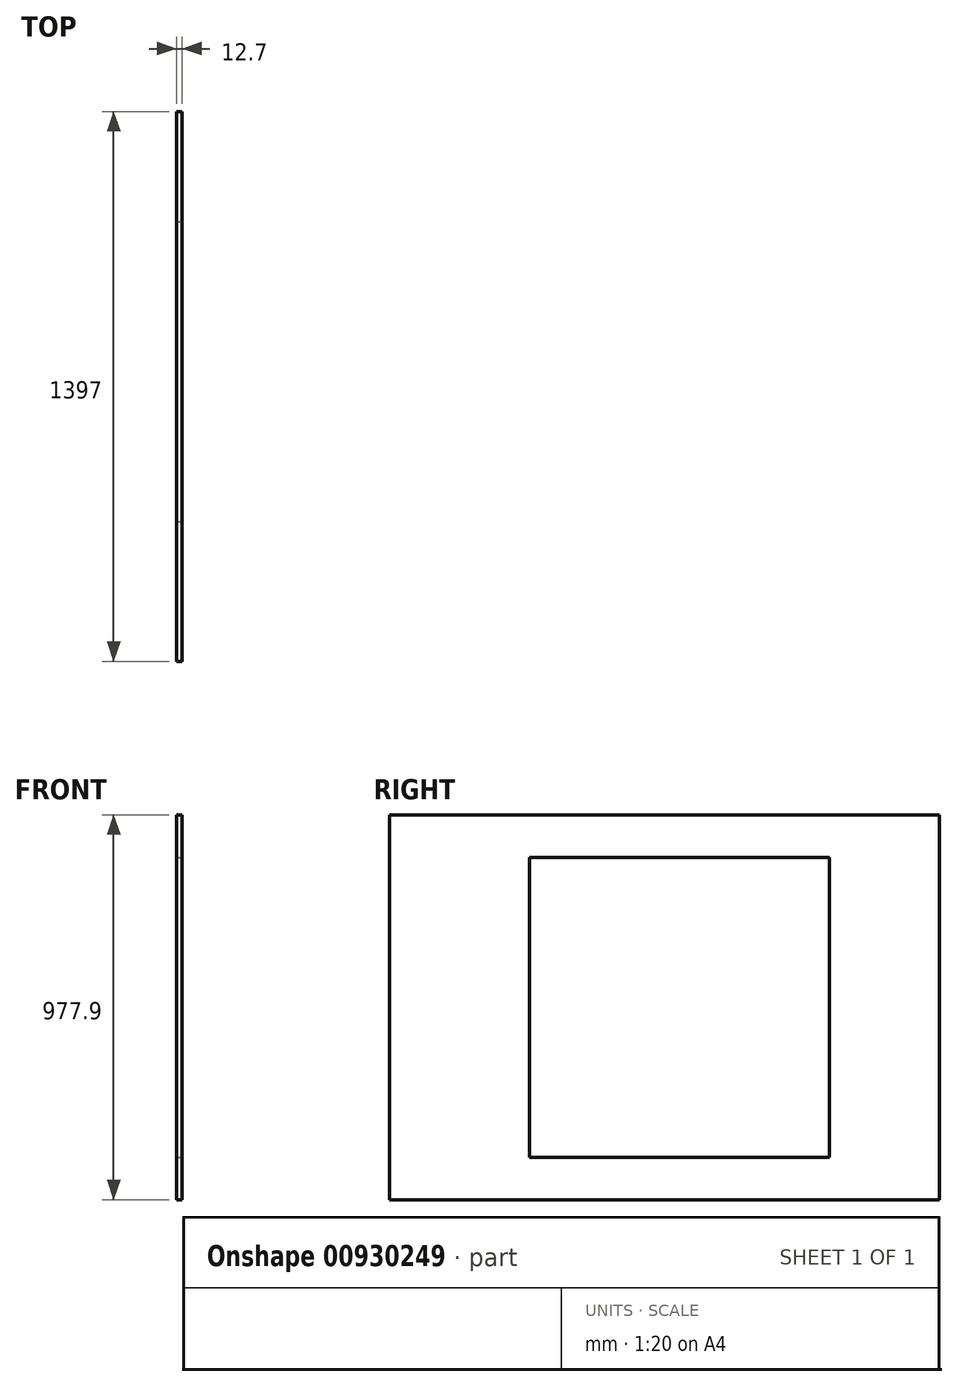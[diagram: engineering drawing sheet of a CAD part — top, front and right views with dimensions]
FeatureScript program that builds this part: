
annotation { "Feature Type Name" : "Feature", "Feature Type Description" : "" }
export const myFeature = defineFeature(function(context is Context, id is Id, definition is map)
    precondition{}
    {
        {
            var Q0;
            Q0=qCreatedBy(makeId("Right.planeOp"),FACE);
            var sketch = newSketch(context, id + "F0", { "sketchPlane" : qUnion([Q0])});
            skLineSegment(sketch, "E0.bottom", {"start": v(698.5, -488.95) * mm, "end": v(-698.5, -488.95) * mm});
            skLineSegment(sketch, "E0.top", {"start": v(698.5, 488.95) * mm, "end": v(-698.5, 488.95) * mm});
            skLineSegment(sketch, "E0.left", {"start": v(698.5, -488.95) * mm, "end": v(698.5, 488.95) * mm});
            skLineSegment(sketch, "E0.right", {"start": v(-698.5, -488.95) * mm, "end": v(-698.5, 488.95) * mm});
            skPoint(sketch, "E0.middle", {"position": v(0, 0) * mm});
            skSolve(sketch);
        }
        {
            var Q0;
            Q0=qSketchRegion(id+"F0",true);
            extrude(context, id + "F1", {"entities" : qUnion([Q0]), "endBound" : BoundingType.SYMMETRIC, "depth" : 12.7 * mm});
        }
        {
            var Q0;
            Q0=makeQuery(id+"F1.opExtrude","CAP_FACE",FACE,{"disambiguationData":[OSD([sQuery(id+"F0.wireOp",EDGE,"E0.bottom"),sQuery(id+"F0.wireOp",EDGE,"E0.top"),sQuery(id+"F0.wireOp",EDGE,"E0.left"),sQuery(id+"F0.wireOp",EDGE,"E0.right")])],"isStart":false});
            var sketch = newSketch(context, id + "F2", { "sketchPlane" : qUnion([Q0])});
            skLineSegment(sketch, "E1.bottom", {"start": v(-342.9, -381) * mm, "end": v(419.1, -381) * mm});
            skLineSegment(sketch, "E1.top", {"start": v(-342.9, 381) * mm, "end": v(419.1, 381) * mm});
            skLineSegment(sketch, "E1.left", {"start": v(-342.9, -381) * mm, "end": v(-342.9, 381) * mm});
            skLineSegment(sketch, "E1.right", {"start": v(419.1, -381) * mm, "end": v(419.1, 381) * mm});
            skSolve(sketch);
        }
        {
            var Q0;
            Q0=qSketchRegion(id+"F2",true);
            extrude(context, id + "F3", {"entities" : qUnion([Q0]), "operationType" : NewBodyOperationType.REMOVE, "endBound" : BoundingType.THROUGH_ALL, "oppositeDirection" : true, "depth" : 25.4 * mm});
        }
    });
